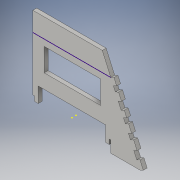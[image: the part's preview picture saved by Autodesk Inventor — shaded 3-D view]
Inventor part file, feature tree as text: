
AUTODESK INVENTOR PART (.ipt)
format: ipt  version: 2016 (Build 200138000, 138)  size: 198,656 bytes
history: native  units: in
note: dims shown in document units (in); Inventor stores cm internally (conversion verified against a paired STEP export)
features: sketch x11, extrude x6
ambient origin geometry x8: Origin, YZ Plane, XZ Plane, XY Plane, X Axis, Y Axis, Z Axis, Center Point
bodies: Solid1 (feature_tree)
feature tree (17):
  extrude  "Extrusion1"  Depth=2.194in
  sketch  "Sketch2"  dims[d5=0.127in d6=0.127in d7=0.0in]
  sketch  "Sketch4"  dims[d14=0.05in d15=0.05in]
  extrude  "Extrusion3"  Depth=0.127in TaperAngle=0.0deg
  sketch  "Sketch10"  dims[d33=1.5in d40=0.7833in]
  sketch  "Sketch11"  dims[d41=0.127in d42=0.0in d43=0.127in d44=0.0in]
  extrude  "Extrusion8"  Depth=0.05in
  extrude  "Extrusion9"  Depth=0.127in
  extrude  "Extrusion10"  Depth=0.7833in
  sketch  "Sketch16"
  sketch  "Sketch17"
  extrude  "Extrusion11"  Depth=0.127in TaperAngle=0.0deg
  sketch  "Sketch1"  dims[d3=0.127in d4=2.194in]
  sketch  "Sketch5"  dims[d16=0.127in d17=0.0in d21=0.7833in]
  sketch  "Sketch13"  dims[d45=0.127in d46=0.0in]
  sketch  "Sketch14"  dims[d47=0.7833in]
  sketch  "Sketch15"  dims[d48=0.127in d49=0.0in]
